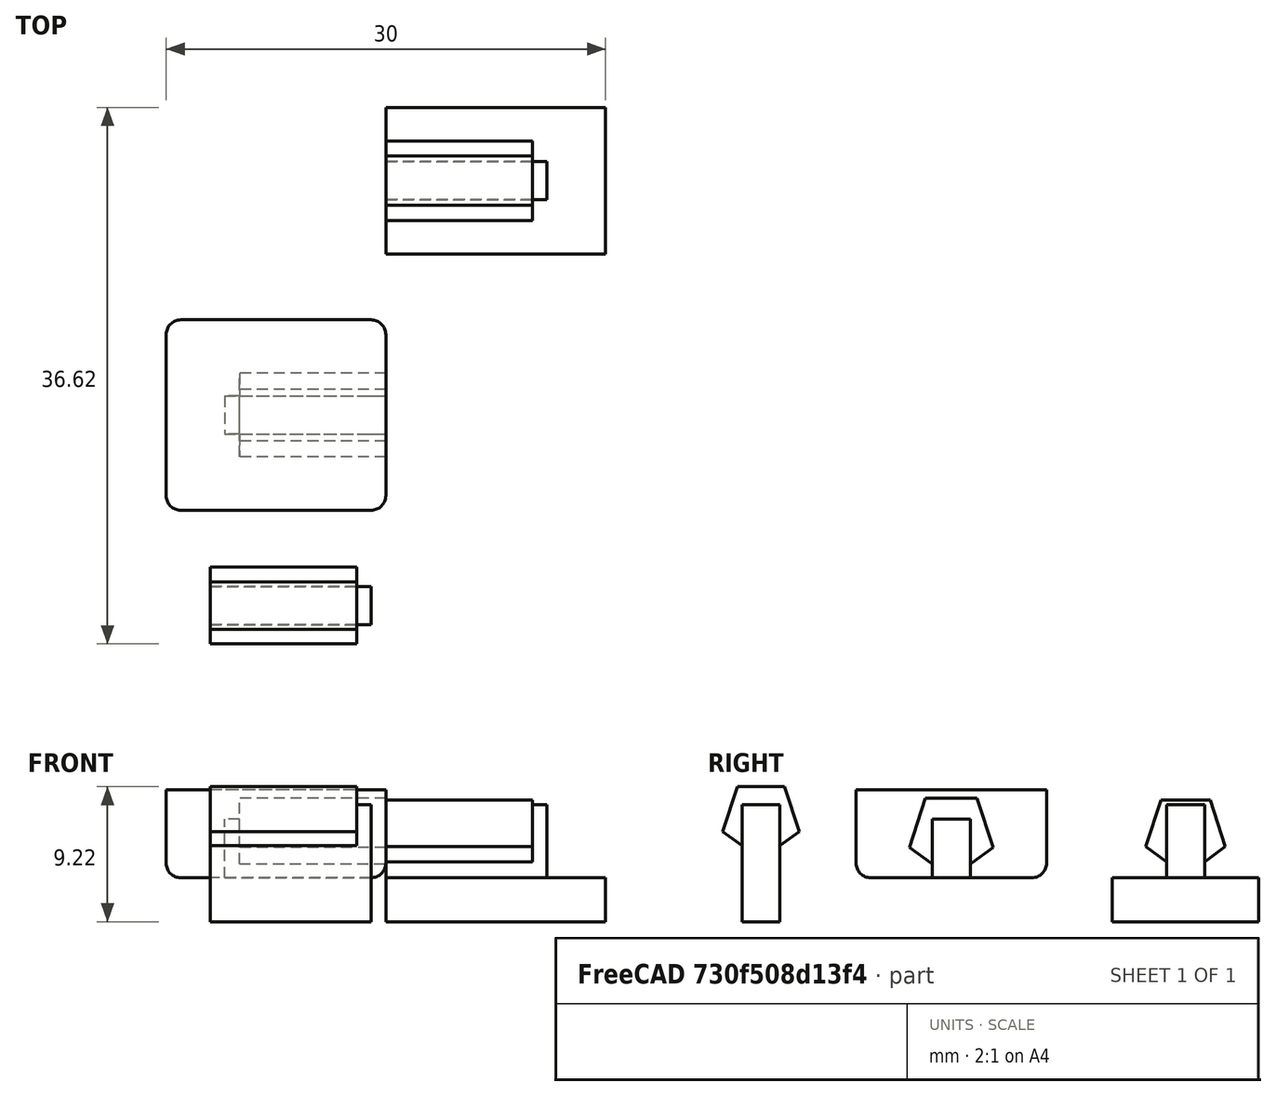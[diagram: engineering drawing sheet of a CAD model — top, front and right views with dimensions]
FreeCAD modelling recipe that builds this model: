
FCSTD DOCUMENT  (FreeCAD 0.18.1R)
Label: key-and-mountpoint
License: All rights reserved
LicenseURL: http://en.wikipedia.org/wiki/All_rights_reserved
objects: Part::Box×5, Part::MultiFuse×4, Part::RegularPolygon×3, Part::Extrusion×3, Part::Fillet×1, Part::Cut×1
note: 17 computed .brp shape members not serialized (recipe doc carries the construction recipe); baked Part::Feature solids carry a one-line shape summary decoded from their .brp

FEATURE [Part::RegularPolygon] RegularPolygon001  label="Regular polygon001"
  AttacherType = Attacher::AttachEngine3D
  Circumradius = 2.85
  Placement = pos=(-3,7,0) rot=(0,0,1;0rad)
  Polygon = 5
FEATURE [Part::Box] Box002  label="Cube002"
  AttacherType = Attacher::AttachEngine3D
  Height = 8
  Length = 11
  Placement = pos=(0,5.7,-3) rot=(0,0,1;0rad)
  Width = 2.6
FEATURE [Part::Extrusion] Extrude001
  Base = -> RegularPolygon001
  Dir = (0,0,1)
  DirMode = 2
  FaceMakerClass = Part::FaceMakerBullseye
  LengthFwd = 10
  LengthRev = 0
  Placement = pos=(0,0,0) rot=(0,1,0;1.5708rad)
  Solid = true
  Symmetric = false
FEATURE [Part::MultiFuse] Fusion001  label="key"
  Placement = pos=(0,1,0) rot=(0,0,1;0rad)
  Shapes = -> [Extrude001,Box002]
FEATURE [Part::RegularPolygon] RegularPolygon002  label="Regular polygon002"
  AttacherType = Attacher::AttachEngine3D
  Circumradius = 3
  Placement = pos=(-3,7,0) rot=(0,0,1;0rad)
  Polygon = 5
FEATURE [Part::Box] Box003  label="Cube003"
  AttacherType = Attacher::AttachEngine3D
  Height = 8
  Length = 11
  Placement = pos=(0,5.7,-4) rot=(0,0,1;0rad)
  Width = 2.6
FEATURE [Part::Extrusion] Extrude002
  Base = -> RegularPolygon002
  Dir = (0,0,1)
  DirMode = 2
  FaceMakerClass = Part::FaceMakerBullseye
  LengthFwd = 10
  LengthRev = 0
  Placement = pos=(0,0,0) rot=(0,1,0;1.5708rad)
  Solid = true
  Symmetric = false
FEATURE [Part::MultiFuse] Fusion002  label="key001"
  Placement = pos=(0,1,0) rot=(0,0,1;0rad)
  Shapes = -> [Extrude002,Box003]
FEATURE [Part::RegularPolygon] RegularPolygon003  label="Regular polygon003"
  AttacherType = Attacher::AttachEngine3D
  Circumradius = 2.75
  Placement = pos=(-3,7,0) rot=(0,0,1;0rad)
  Polygon = 5
FEATURE [Part::Box] Box004  label="Cube004"
  AttacherType = Attacher::AttachEngine3D
  Height = 8
  Length = 11
  Placement = pos=(0,5.7,-4) rot=(0,0,1;0rad)
  Width = 2.6
FEATURE [Part::Extrusion] Extrude003
  Base = -> RegularPolygon003
  Dir = (0,0,1)
  DirMode = 2
  FaceMakerClass = Part::FaceMakerBullseye
  LengthFwd = 10
  LengthRev = 0
  Placement = pos=(0,0,0) rot=(0,1,0;1.5708rad)
  Solid = true
  Symmetric = false
FEATURE [Part::MultiFuse] Fusion003  label="keymaster"
  Placement = pos=(-12,-28,1) rot=(0,0,1;0rad)
  Shapes = -> [Extrude003,Box004]
FEATURE [Part::Box] Box005  label="Cube005"
  AttacherType = Attacher::AttachEngine3D
  Height = 3
  Length = 15
  Placement = pos=(0,3,-3) rot=(0,0,1;0rad)
  Width = 10
FEATURE [Part::MultiFuse] Fusion  label="keypart test"
  Shapes = -> [Fusion001,Box005]
FEATURE [Part::Box] Box  label="Cube"
  AttacherType = Attacher::AttachEngine3D
  Height = 6
  Length = 15
  Placement = pos=(0,1.5,0) rot=(0,0,1;0rad)
  Width = 13
FEATURE [Part::Fillet] Fillet
  Base = -> Box
  Edges = 8 edges r=1: [Edge1,Edge3,Edge4,Edge5,Edge7,Edge8,Edge9,Edge11]
FEATURE [Part::Cut] Cut
  Base = -> Fillet
  Placement = pos=(0,0,0) rot=(0,0,1;3.14159rad)
  Tool = -> Fusion002
